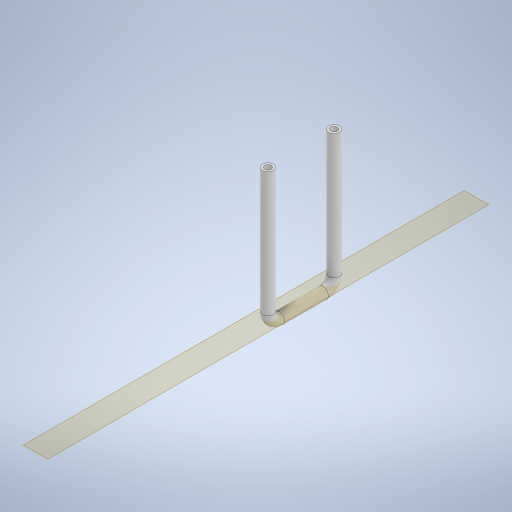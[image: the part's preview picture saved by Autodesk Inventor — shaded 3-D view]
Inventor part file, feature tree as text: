
AUTODESK INVENTOR PART (.ipt)
format: ipt  version: 2024 (Build 280153000, 153)  size: 283,648 bytes
history: native  units: in
note: dims shown in document units (in); Inventor stores cm internally (conversion verified against a paired STEP export)
features: sketch x3, other x2, extrude x1, plane x1
ambient origin geometry x8: Origin, YZ Plane, XZ Plane, XY Plane, X Axis, Y Axis, Z Axis, Center Point
bodies: Solid1 (feature_tree)
feature tree (7):
  extrude  "Extrusion1"  Depth=0.9843in
  plane  "Work Plane2"
  other  "Bend Part1"
  other  "Bend Part2"
  sketch  "Sketch1"  dims[d0=0.5906in d1=0.9843in]
  sketch  "Sketch3"  dims[d2=27.4803in d3=0.0in]
  sketch  "Sketch4"  dims[d7=11.811in d8=11.811in d9=0.5in d10=90.0deg d11=11.811in d12=0.5in d13=90.0deg]
